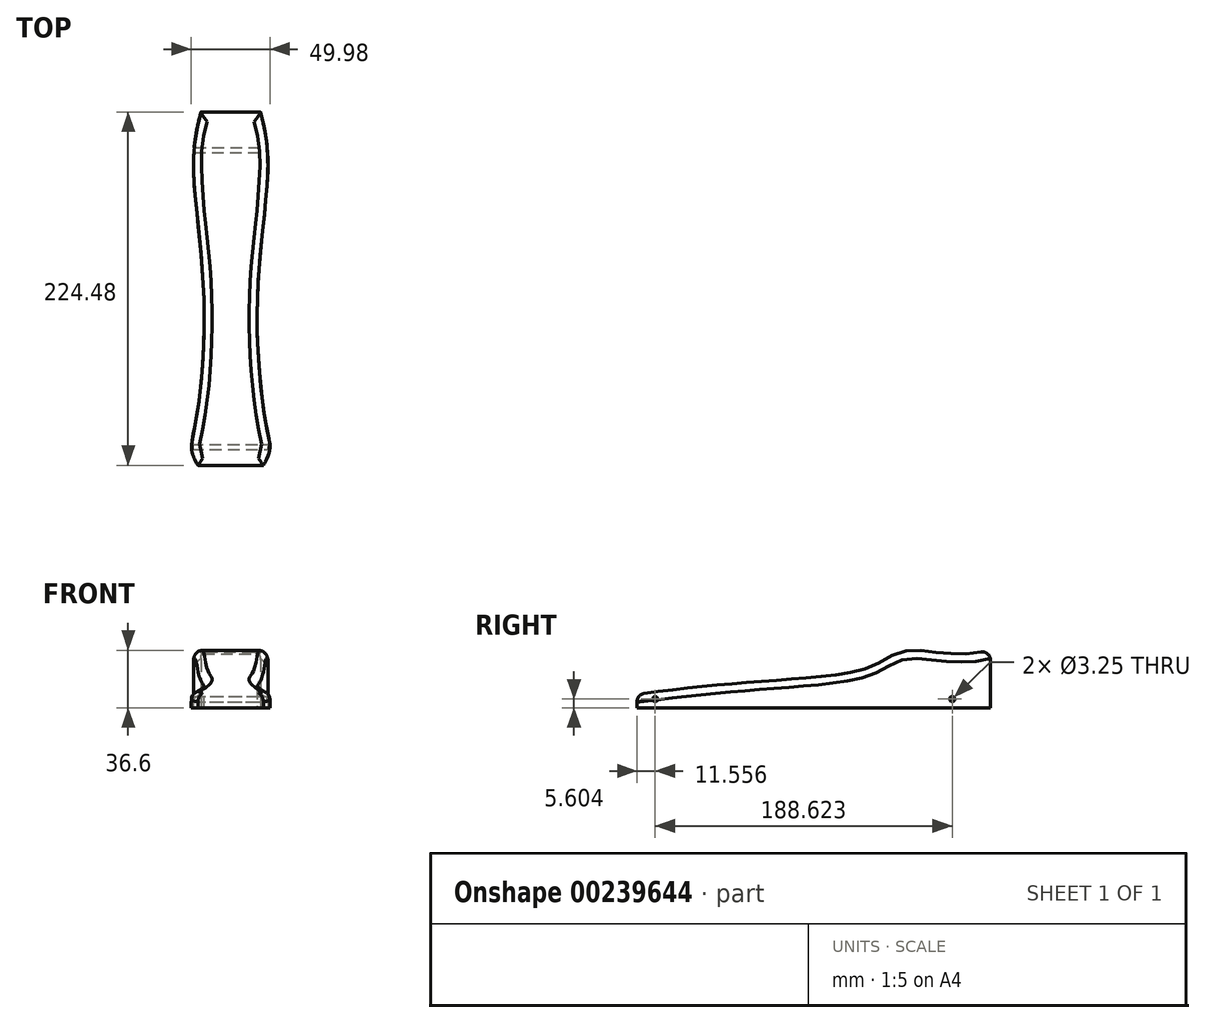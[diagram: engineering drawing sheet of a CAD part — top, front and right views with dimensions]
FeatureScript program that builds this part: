
annotation { "Feature Type Name" : "Feature", "Feature Type Description" : "" }
export const myFeature = defineFeature(function(context is Context, id is Id, definition is map)
    precondition{}
    {
        {
            var Q0;
            Q0=qCreatedBy(makeId("Right.planeOp"),FACE);
            var sketch = newSketch(context, id + "F0", { "sketchPlane" : qUnion([Q0])});
            skLineSegment(sketch, "E0", {"start": v(92.52, 0) * mm, "end": v(92.52, 53.3) * mm, "construction": true});
            skLineSegment(sketch, "E1", {"start": v(92.52, 53.3) * mm, "end": v(-144.23, 7.23) * mm, "construction": true});
            skLineSegment(sketch, "E2", {"start": v(-144.23, 7.23) * mm, "end": v(-144.23, 0) * mm, "construction": true});
            skFitSpline(sketch, "E3", {"points": [v(92.52, 38.72) * mm, v(36.5, 36.48) * mm, v(17.5, 28.67) * mm, v(-8.04, 21.31) * mm, v(-144.23, 7.23) * mm], "startDerivative": vector(-237.77, -105.78) * mm, "endDerivative": vector(-399.85, -65.81) * mm});
            skLineSegment(sketch, "E4", {"start": v(-144.23, 7.23) * mm, "end": v(-183.22, 7.23) * mm});
            skLineSegment(sketch, "E5", {"start": v(-183.22, 7.23) * mm, "end": v(-183.22, 65.38) * mm});
            skLineSegment(sketch, "E6", {"start": v(-183.22, 65.38) * mm, "end": v(103.21, 65.38) * mm});
            skLineSegment(sketch, "E7", {"start": v(103.21, 65.38) * mm, "end": v(103.21, 38.72) * mm});
            skLineSegment(sketch, "E8", {"start": v(103.21, 38.72) * mm, "end": v(92.52, 38.72) * mm});
            skCircle(sketch, "E9", {"center": v(63.95, 5.6) * mm, "radius": 1.63 * mm});
            skCircle(sketch, "E10", {"center": v(-124.67, 5.6) * mm, "radius": 1.63 * mm});
            skSolve(sketch);
        }
        {
            var Q0;
            Q0=qCreatedBy(makeId("Top.planeOp"),FACE);
            var sketch = newSketch(context, id + "F1", { "sketchPlane" : qUnion([Q0])});
            skFitSpline(sketch, "E11", {"points": [v(18.87, 88.25) * mm, v(23.67, 56.12) * mm, v(16.95, -31.16) * mm, v(23.19, -113.64) * mm, v(20.79, -136.17) * mm], "startDerivative": vector(36.62, -142.8) * mm, "endDerivative": vector(-111.48, -183.73) * mm});
            skFitSpline(sketch, "E12.MirrorCS", {"points": [v(-18.87, 88.25) * mm, v(-23.67, 56.12) * mm, v(-16.95, -31.16) * mm, v(-23.19, -113.64) * mm, v(-20.79, -136.17) * mm], "startDerivative": vector(-36.62, -142.8) * mm, "endDerivative": vector(111.48, -183.73) * mm});
            skLineSegment(sketch, "E13", {"start": v(18.87, 88.25) * mm, "end": v(-18.87, 88.25) * mm});
            skLineSegment(sketch, "E14", {"start": v(-20.79, -136.17) * mm, "end": v(20.79, -136.17) * mm});
            skSolve(sketch);
        }
        {
            var Q0;
            Q0 = qSketchRegion(id + "F1", true);
            extrude(context, id + "F2", {"entities" : qUnion([Q0]), "depth" : 57.4 * mm});
        }
        {
            var Q0;
            Q0 = qSketchRegion(id + "F0", true);
            extrude(context, id + "F3", {"entities" : qUnion([Q0]), "operationType" : NewBodyOperationType.REMOVE, "oppositeDirection" : true, "depth" : 83.31 * mm, "symmetric" : true});
        }
        {
            var Q0;
            Q0=makeQuery(id+"F3.boolean.opBoolean","COPY",FACE,{"derivedFrom":makeQuery(id+"F3.opExtrude","SWEPT_FACE",FACE,{"disambiguationData":[OSD([sQuery(id+"F0.wireOp",EDGE,"E3")])]})});
            fillet(context, id + "F4", {"entities" : qUnion([Q0]), "radius" : 5.08 * mm, "tangentPropagation" : true, "allowEdgeOverflow" : false});
        }
    });
